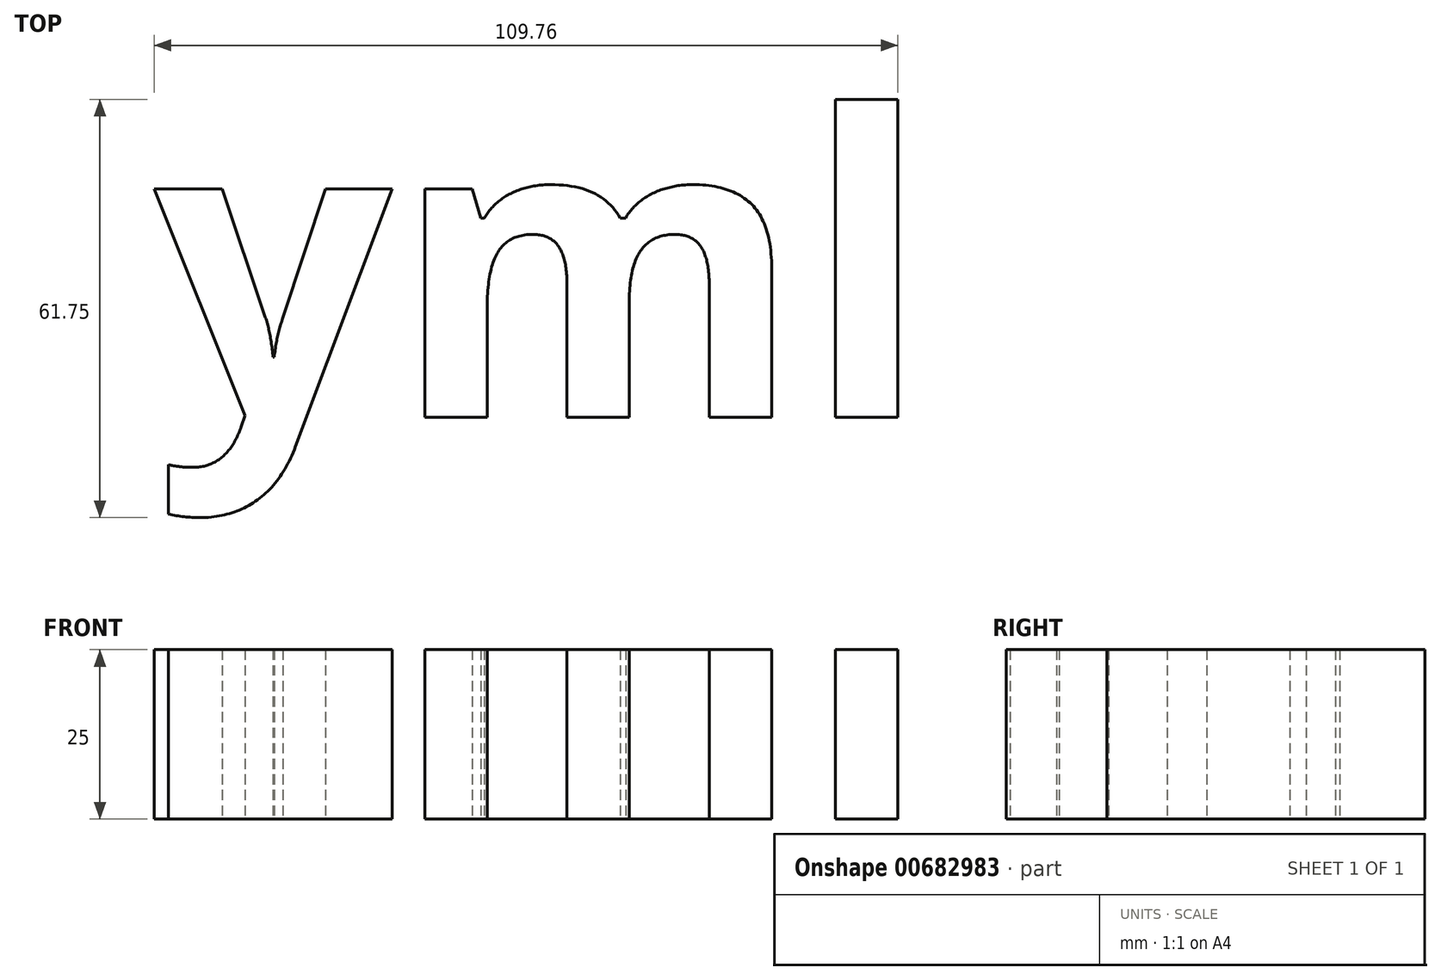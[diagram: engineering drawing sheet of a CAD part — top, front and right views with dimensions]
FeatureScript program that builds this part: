
annotation { "Feature Type Name" : "Feature", "Feature Type Description" : "" }
export const myFeature = defineFeature(function(context is Context, id is Id, definition is map)
    precondition{}
    {
        {
            var Q0;
            Q0=qCreatedBy(makeId("Top.planeOp"),FACE);
            var sketch = newSketch(context, id + "F0", { "sketchPlane" : qUnion([Q0])});
            skText(sketch, "E0", { "text": "yml", "fontName": "OpenSans-Bold.ttf"});
            const initialGuessF0  = {"E0": [0, -0.04445, 1, 0, 0.04445]};
            skSetInitialGuess(sketch, initialGuessF0);
            skSolve(sketch);
        }
        {
            var Q0;
            Q0 = qSketchRegion(id + "F0", true);
            extrude(context, id + "F1", {"entities" : qUnion([Q0]), "depth" : 25 * mm, "offsetDistance" : 25 * mm});
        }
    });
